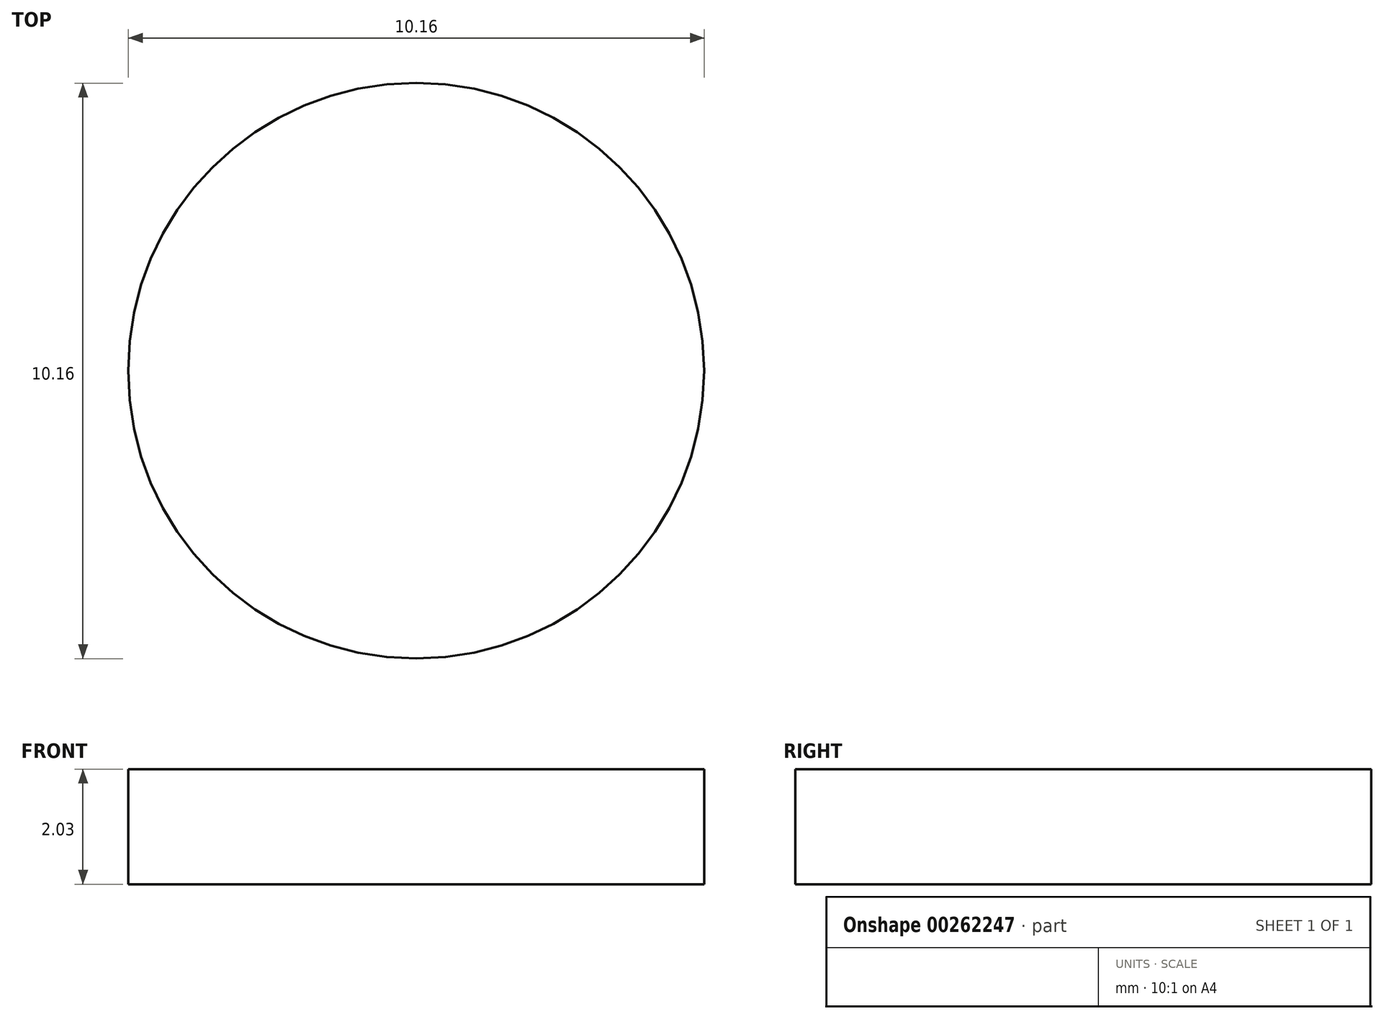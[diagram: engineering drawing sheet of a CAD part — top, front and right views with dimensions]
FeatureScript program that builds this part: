
annotation { "Feature Type Name" : "Feature", "Feature Type Description" : "" }
export const myFeature = defineFeature(function(context is Context, id is Id, definition is map)
    precondition{}
    {
        {
            var Q0;
            Q0=qCreatedBy(makeId("Top.planeOp"),FACE);
            var sketch = newSketch(context, id + "F0", { "sketchPlane" : qUnion([Q0])});
            skCircle(sketch, "E0", {"center": v(-24.84, 24.27) * mm, "radius": 5.08 * mm});
            skSolve(sketch);
        }
        {
            var Q0;
            Q0 = qSketchRegion(id + "F0", true);
            extrude(context, id + "F1", {"entities" : qUnion([Q0]), "depth" : 2.03 * mm});
        }
    });
